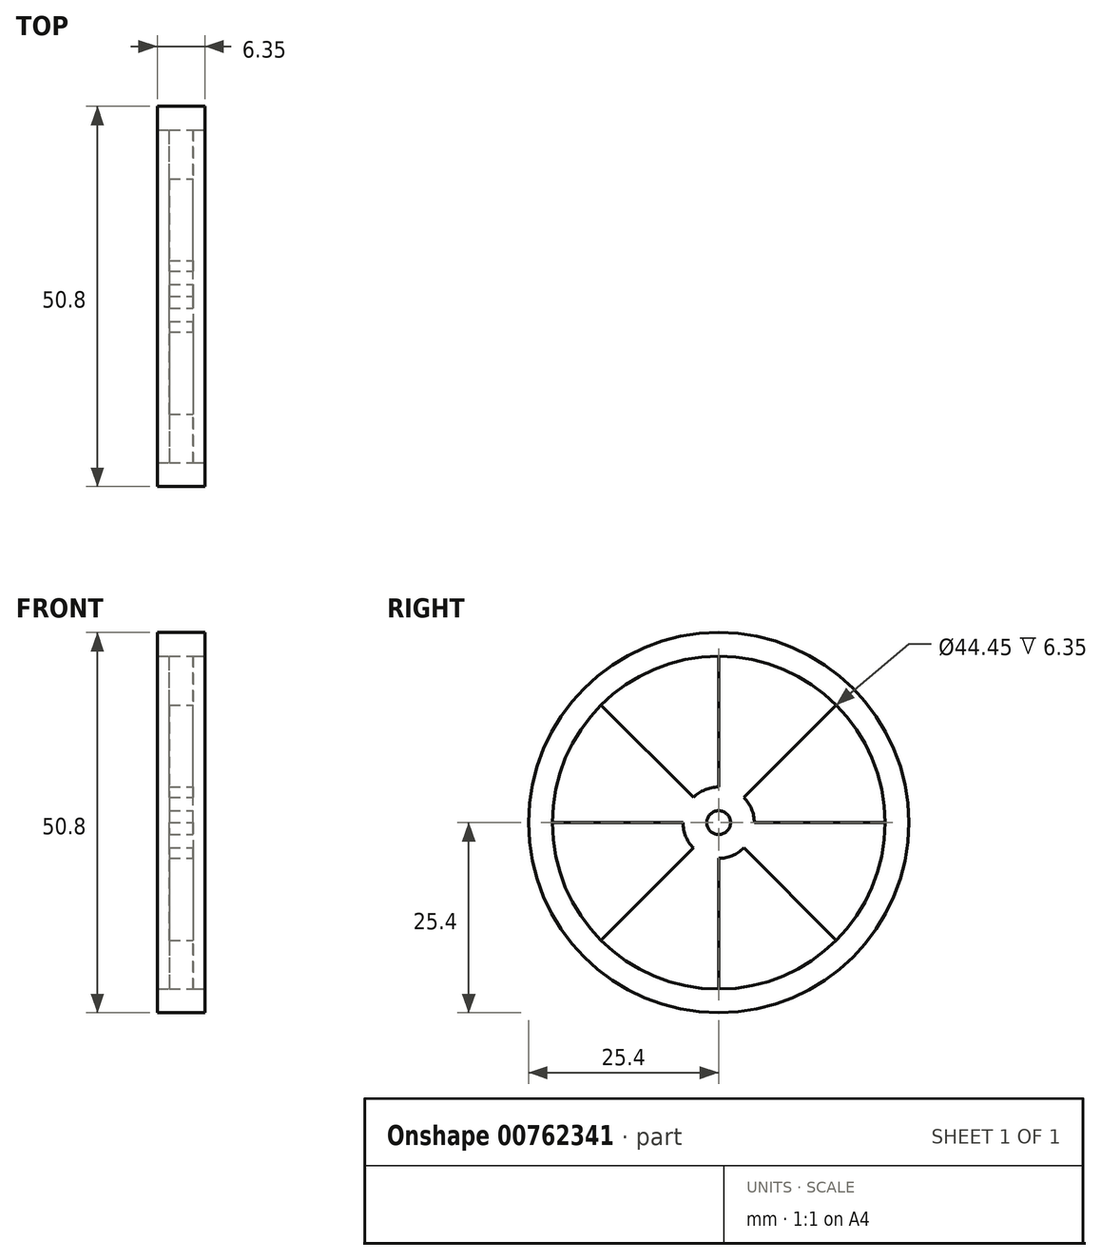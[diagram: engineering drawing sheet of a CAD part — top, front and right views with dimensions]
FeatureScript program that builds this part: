
annotation { "Feature Type Name" : "Feature", "Feature Type Description" : "" }
export const myFeature = defineFeature(function(context is Context, id is Id, definition is map)
    precondition{}
    {
        {
            var Q0;
            Q0=qCreatedBy(makeId("Right.planeOp"),FACE);
            var sketch = newSketch(context, id + "F0", { "sketchPlane" : qUnion([Q0])});
            skCircle(sketch, "E0", {"center": v(0, 0) * mm, "radius": 25.4 * mm});
            skSolve(sketch);
        }
        {
            var Q0;
            Q0=makeQuery(id+"F0.imprint","IMPRINT",FACE,{"disambiguationData":[TD([[makeQuery(id+"F0.imprint","IMPRINT",EDGE,{"derivedFrom":sQuery(id+"F0.wireOp",EDGE,"E0")}),1.0]])]});
            extrude(context, id + "F1", {"entities" : qUnion([Q0]), "depth" : 6.35 * mm, "offsetDistance" : 25.4 * mm});
        }
        {
            var Q0;
            Q0=makeQuery(id+"F1.opExtrude","CAP_FACE",FACE,{"disambiguationData":[OSD([sQuery(id+"F0.wireOp",EDGE,"E0")])],"isStart":false});
            var sketch = newSketch(context, id + "F2", { "sketchPlane" : qUnion([Q0])});
            skCircle(sketch, "E1.0", {"center": v(0, 0) * mm, "radius": 22.22 * mm});
            skCircle(sketch, "E2.0", {"center": v(0, 0) * mm, "radius": 4.76 * mm});
            skCircle(sketch, "E3.0", {"center": v(0, 0) * mm, "radius": 1.59 * mm});
            skLineSegment(sketch, "E4", {"start": v(0, 4.76) * mm, "end": v(0, 22.22) * mm});
            skLineSegment(sketch, "E5.1.0", {"start": v(-3.37, 3.37) * mm, "end": v(-15.72, 15.72) * mm});
            skLineSegment(sketch, "E5.2.0", {"start": v(-4.76, 0) * mm, "end": v(-22.22, 0) * mm});
            skLineSegment(sketch, "E5.3.0", {"start": v(-3.37, -3.37) * mm, "end": v(-15.72, -15.72) * mm});
            skLineSegment(sketch, "E5.4.0", {"start": v(0, -4.76) * mm, "end": v(0, -22.22) * mm});
            skLineSegment(sketch, "E5.5.0", {"start": v(3.37, -3.37) * mm, "end": v(15.72, -15.72) * mm});
            skLineSegment(sketch, "E5.6.0", {"start": v(4.76, 0) * mm, "end": v(22.22, 0) * mm});
            skLineSegment(sketch, "E5.7.0", {"start": v(3.37, 3.37) * mm, "end": v(15.72, 15.72) * mm});
            skSolve(sketch);
        }
        {
            var Q0;
            {var subQ0=sQuery(id+"F2.wireOp",EDGE,"E5.1.0");Q0=makeQuery(id+"F2.imprint","IMPRINT",FACE,{"disambiguationData":[TD([[makeQuery(id+"F2.imprint","IMPRINT",EDGE,{"derivedFrom":subQ0}),1.0]])]});}
            var Q1;
            {var subQ0=sQuery(id+"F2.wireOp",EDGE,"E5.3.0");Q1=makeQuery(id+"F2.imprint","IMPRINT",FACE,{"disambiguationData":[TD([[makeQuery(id+"F2.imprint","IMPRINT",EDGE,{"derivedFrom":subQ0}),1.0]])]});}
            var Q2;
            {var subQ0=sQuery(id+"F2.wireOp",EDGE,"E5.5.0");Q2=makeQuery(id+"F2.imprint","IMPRINT",FACE,{"disambiguationData":[TD([[makeQuery(id+"F2.imprint","IMPRINT",EDGE,{"derivedFrom":subQ0}),1.0]])]});}
            var Q3;
            {var subQ0=sQuery(id+"F2.wireOp",EDGE,"E4");Q3=makeQuery(id+"F2.imprint","IMPRINT",FACE,{"disambiguationData":[TD([[makeQuery(id+"F2.imprint","IMPRINT",EDGE,{"derivedFrom":subQ0}),-1.0]])]});}
            var Q4;
            Q4=makeQuery(id+"F2.imprint","IMPRINT",FACE,{"disambiguationData":[TD([[makeQuery(id+"F2.imprint","IMPRINT",EDGE,{"derivedFrom":sQuery(id+"F2.wireOp",EDGE,"E3.0")}),-1.0]])]});
            extrude(context, id + "F3", {"entities" : qUnion([Q0, Q1, Q2, Q3, Q4]), "operationType" : NewBodyOperationType.REMOVE, "oppositeDirection" : true, "depth" : 3.17 * mm, "offsetDistance" : 25.4 * mm});
        }
        {
            var Q0;
            {var subQ0=sQuery(id+"F2.wireOp",EDGE,"E4");Q0=makeQuery(id+"F2.imprint","IMPRINT",FACE,{"disambiguationData":[TD([[makeQuery(id+"F2.imprint","IMPRINT",EDGE,{"derivedFrom":subQ0}),1.0]])]});}
            var Q1;
            {var subQ0=sQuery(id+"F2.wireOp",EDGE,"E5.6.0");Q1=makeQuery(id+"F2.imprint","IMPRINT",FACE,{"disambiguationData":[TD([[makeQuery(id+"F2.imprint","IMPRINT",EDGE,{"derivedFrom":subQ0}),1.0]])]});}
            var Q2;
            {var subQ0=sQuery(id+"F2.wireOp",EDGE,"E5.4.0");Q2=makeQuery(id+"F2.imprint","IMPRINT",FACE,{"disambiguationData":[TD([[makeQuery(id+"F2.imprint","IMPRINT",EDGE,{"derivedFrom":subQ0}),1.0]])]});}
            var Q3;
            {var subQ0=sQuery(id+"F2.wireOp",EDGE,"E5.2.0");Q3=makeQuery(id+"F2.imprint","IMPRINT",FACE,{"disambiguationData":[TD([[makeQuery(id+"F2.imprint","IMPRINT",EDGE,{"derivedFrom":subQ0}),1.0]])]});}
            var Q4;
            Q4=makeQuery(id+"F2.imprint","IMPRINT",FACE,{"disambiguationData":[TD([[makeQuery(id+"F2.imprint","IMPRINT",EDGE,{"derivedFrom":sQuery(id+"F2.wireOp",EDGE,"E3.0")}),1.0]])]});
            extrude(context, id + "F4", {"entities" : qUnion([Q0, Q1, Q2, Q3, Q4]), "operationType" : NewBodyOperationType.REMOVE, "oppositeDirection" : true, "depth" : 1.59 * mm, "offsetDistance" : 25.4 * mm});
        }
        {
            var Q0;
            Q0=makeQuery(id+"F1.opExtrude","CAP_FACE",FACE,{"disambiguationData":[OSD([sQuery(id+"F0.wireOp",EDGE,"E0")])],"isStart":true});
            var sketch = newSketch(context, id + "F5", { "sketchPlane" : qUnion([Q0])});
            skCircle(sketch, "E6.0", {"center": v(0, 0) * mm, "radius": 22.22 * mm});
            skCircle(sketch, "E7.0", {"center": v(0, 0) * mm, "radius": 4.76 * mm});
            skCircle(sketch, "E8.0", {"center": v(0, 0) * mm, "radius": 1.59 * mm});
            skLineSegment(sketch, "E9", {"start": v(0, 4.76) * mm, "end": v(0, 22.22) * mm});
            skLineSegment(sketch, "E10.1.0", {"start": v(-3.37, 3.37) * mm, "end": v(-15.72, 15.72) * mm});
            skLineSegment(sketch, "E10.2.0", {"start": v(-4.76, 0) * mm, "end": v(-22.22, 0) * mm});
            skLineSegment(sketch, "E10.3.0", {"start": v(-3.37, -3.37) * mm, "end": v(-15.72, -15.72) * mm});
            skLineSegment(sketch, "E10.4.0", {"start": v(0, -4.76) * mm, "end": v(0, -22.22) * mm});
            skLineSegment(sketch, "E10.5.0", {"start": v(3.37, -3.37) * mm, "end": v(15.72, -15.72) * mm});
            skLineSegment(sketch, "E10.6.0", {"start": v(4.76, 0) * mm, "end": v(22.22, 0) * mm});
            skLineSegment(sketch, "E10.7.0", {"start": v(3.37, 3.37) * mm, "end": v(15.72, 15.72) * mm});
            skSolve(sketch);
        }
        {
            var Q0;
            {var subQ0=sQuery(id+"F5.wireOp",EDGE,"E9");Q0=makeQuery(id+"F5.imprint","IMPRINT",FACE,{"disambiguationData":[TD([[makeQuery(id+"F5.imprint","IMPRINT",EDGE,{"derivedFrom":subQ0}),-1.0]])]});}
            var Q1;
            {var subQ0=sQuery(id+"F5.wireOp",EDGE,"E10.5.0");Q1=makeQuery(id+"F5.imprint","IMPRINT",FACE,{"disambiguationData":[TD([[makeQuery(id+"F5.imprint","IMPRINT",EDGE,{"derivedFrom":subQ0}),1.0]])]});}
            var Q2;
            {var subQ0=sQuery(id+"F5.wireOp",EDGE,"E10.3.0");Q2=makeQuery(id+"F5.imprint","IMPRINT",FACE,{"disambiguationData":[TD([[makeQuery(id+"F5.imprint","IMPRINT",EDGE,{"derivedFrom":subQ0}),1.0]])]});}
            var Q3;
            {var subQ0=sQuery(id+"F5.wireOp",EDGE,"E10.1.0");Q3=makeQuery(id+"F5.imprint","IMPRINT",FACE,{"disambiguationData":[TD([[makeQuery(id+"F5.imprint","IMPRINT",EDGE,{"derivedFrom":subQ0}),1.0]])]});}
            var Q4;
            Q4=makeQuery(id+"F5.imprint","IMPRINT",FACE,{"disambiguationData":[TD([[makeQuery(id+"F5.imprint","IMPRINT",EDGE,{"derivedFrom":sQuery(id+"F5.wireOp",EDGE,"E8.0")}),1.0]])]});
            var Q5;
            Q5=makeQuery(id+"F3.boolean.opBoolean","COPY",FACE,{"derivedFrom":makeQuery(id+"F3.opExtrude","CAP_FACE",FACE,{"disambiguationData":[OSD([sQuery(id+"F2.wireOp",EDGE,"E1.0"),sQuery(id+"F2.wireOp",EDGE,"E2.0"),sQuery(id+"F2.wireOp",EDGE,"E3.0"),sQuery(id+"F2.wireOp",EDGE,"E4"),sQuery(id+"F2.wireOp",EDGE,"E5.1.0"),sQuery(id+"F2.wireOp",EDGE,"E5.2.0"),sQuery(id+"F2.wireOp",EDGE,"E5.3.0"),sQuery(id+"F2.wireOp",EDGE,"E5.4.0"),sQuery(id+"F2.wireOp",EDGE,"E5.5.0"),sQuery(id+"F2.wireOp",EDGE,"E5.6.0"),sQuery(id+"F2.wireOp",EDGE,"E5.7.0")])],"isStart":false})});
            var Q6;
            Q6=makeQuery(id+"F4.boolean.opBoolean","COPY",FACE,{"derivedFrom":makeQuery(id+"F4.opExtrude","CAP_FACE",FACE,{"disambiguationData":[OSD([sQuery(id+"F2.wireOp",EDGE,"E3.0")])],"isStart":false})});
            extrude(context, id + "F6", {"entities" : qUnion([Q0, Q1, Q2, Q3, Q4, Q5, Q6]), "operationType" : NewBodyOperationType.REMOVE, "oppositeDirection" : true, "depth" : 1.59 * mm, "offsetDistance" : 25.4 * mm});
        }
        {
            var Q0;
            {var subQ0=sQuery(id+"F5.wireOp",EDGE,"E9");Q0=makeQuery(id+"F5.imprint","IMPRINT",FACE,{"disambiguationData":[TD([[makeQuery(id+"F5.imprint","IMPRINT",EDGE,{"derivedFrom":subQ0}),1.0]])]});}
            var Q1;
            {var subQ0=sQuery(id+"F5.wireOp",EDGE,"E10.2.0");Q1=makeQuery(id+"F5.imprint","IMPRINT",FACE,{"disambiguationData":[TD([[makeQuery(id+"F5.imprint","IMPRINT",EDGE,{"derivedFrom":subQ0}),1.0]])]});}
            var Q2;
            {var subQ0=sQuery(id+"F5.wireOp",EDGE,"E10.4.0");Q2=makeQuery(id+"F5.imprint","IMPRINT",FACE,{"disambiguationData":[TD([[makeQuery(id+"F5.imprint","IMPRINT",EDGE,{"derivedFrom":subQ0}),1.0]])]});}
            var Q3;
            {var subQ0=sQuery(id+"F5.wireOp",EDGE,"E10.6.0");Q3=makeQuery(id+"F5.imprint","IMPRINT",FACE,{"disambiguationData":[TD([[makeQuery(id+"F5.imprint","IMPRINT",EDGE,{"derivedFrom":subQ0}),1.0]])]});}
            var Q4;
            Q4=makeQuery(id+"F5.imprint","IMPRINT",FACE,{"disambiguationData":[TD([[makeQuery(id+"F5.imprint","IMPRINT",EDGE,{"derivedFrom":sQuery(id+"F5.wireOp",EDGE,"E8.0")}),-1.0]])]});
            extrude(context, id + "F7", {"entities" : qUnion([Q0, Q1, Q2, Q3, Q4]), "operationType" : NewBodyOperationType.REMOVE, "oppositeDirection" : true, "depth" : 3.17 * mm, "offsetDistance" : 25.4 * mm});
        }
    });
